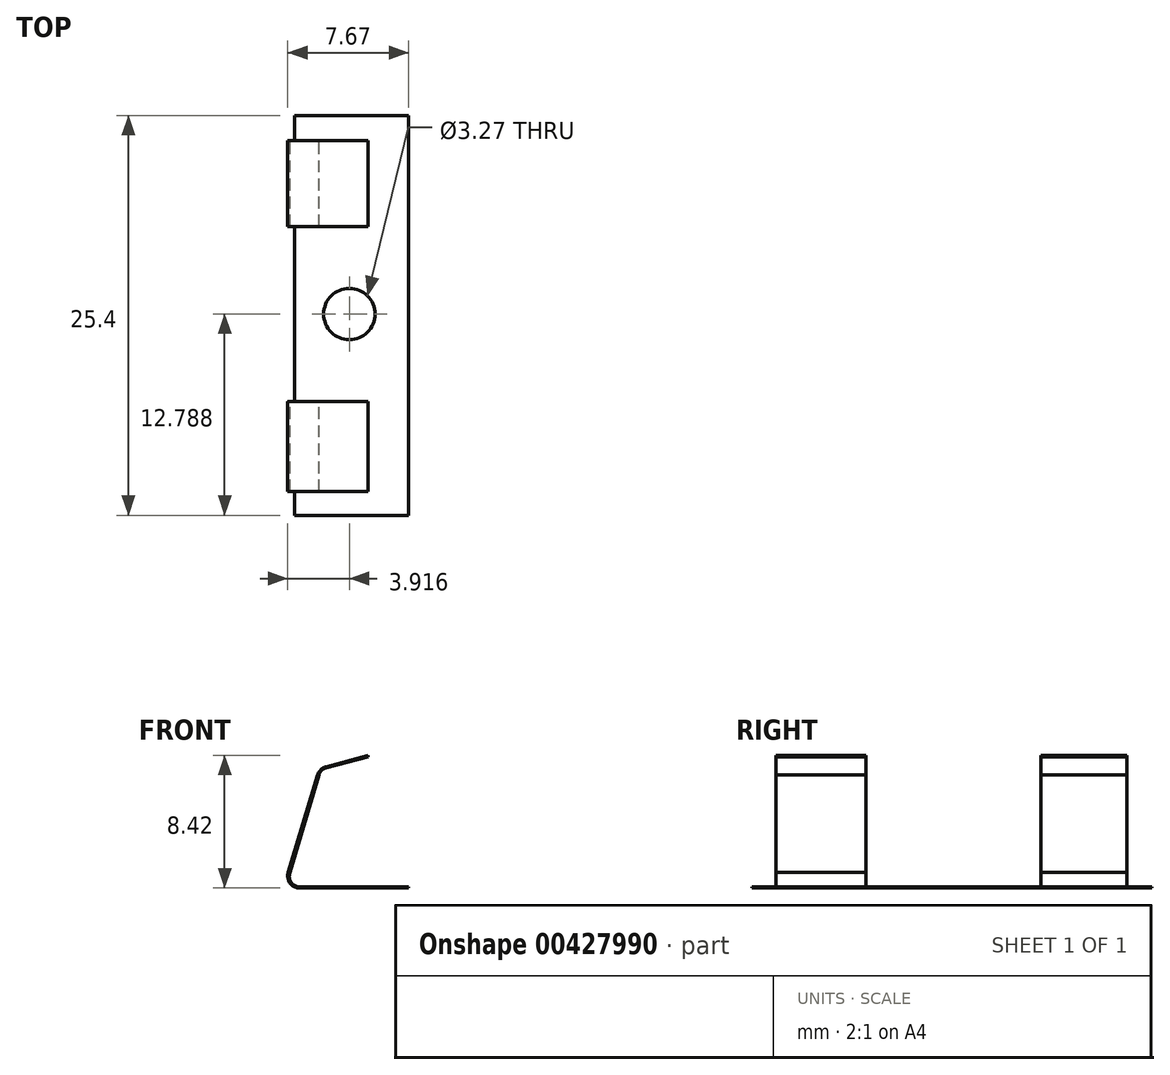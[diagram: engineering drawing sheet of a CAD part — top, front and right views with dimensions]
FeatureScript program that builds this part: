
annotation { "Feature Type Name" : "Feature", "Feature Type Description" : "" }
export const myFeature = defineFeature(function(context is Context, id is Id, definition is map)
    precondition{}
    {
        {
            var Q0;
            Q0=qCreatedBy(makeId("Front.planeOp"),FACE);
            var sketch = newSketch(context, id + "F0", { "sketchPlane" : qUnion([Q0])});
            skLineSegment(sketch, "E0", {"start": v(0, 0) * mm, "end": v(-0.56, 0) * mm});
            skLineSegment(sketch, "E1", {"start": v(-1.3, 0.98) * mm, "end": v(0.59, 7.2) * mm});
            skLineSegment(sketch, "E2", {"start": v(0, 0) * mm, "end": v(6.35, 0) * mm});
            skLineSegment(sketch, "E3", {"start": v(1.12, 7.7) * mm, "end": v(3.78, 8.42) * mm});
            skPoint(sketch, "E4.visualSharp", {"position": v(0.7, 7.6) * mm});
            skArc(sketch, "E4.filletArc", {"start": v(1.12, 7.7) * mm, "mid": v(0.79, 7.52) * mm, "end": v(0.59, 7.2) * mm});
            skPoint(sketch, "E5.visualSharp", {"position": v(-1.59, 0) * mm});
            skArc(sketch, "E5.filletArc", {"start": v(-1.3, 0.98) * mm, "mid": v(-1.17, 0.3) * mm, "end": v(-0.56, 0) * mm});
            skLineSegment(sketch, "E6", {"start": v(6.35, 0) * mm, "end": v(6.35, 0.08) * mm});
            skLineSegment(sketch, "E7", {"start": v(3.78, 8.42) * mm, "end": v(3.78, 8.34) * mm});
            skLineSegment(sketch, "E8", {"start": v(3.78, 8.34) * mm, "end": v(1.12, 7.63) * mm});
            skLineSegment(sketch, "E9", {"start": v(6.35, 0.08) * mm, "end": v(-0.56, 0.08) * mm});
            skArc(sketch, "E10", {"start": v(-1.17, 0.98) * mm, "mid": v(-1.1, 0.37) * mm, "end": v(-0.56, 0.08) * mm});
            skPoint(sketch, "E10.startSnap0", {"position": v(-1.17, 0.3) * mm});
            skArc(sketch, "E11", {"start": v(1.12, 7.63) * mm, "mid": v(0.83, 7.47) * mm, "end": v(0.66, 7.2) * mm});
            skLineSegment(sketch, "E12", {"start": v(0.66, 7.2) * mm, "end": v(-1.17, 0.98) * mm});
            skSolve(sketch);
        }
        {
            var Q0;
            Q0=makeQuery(id+"F0.imprint","IMPRINT",FACE,{"disambiguationData":[TD([[makeQuery(id+"F0.imprint","IMPRINT",EDGE,{"derivedFrom":sQuery(id+"F0.wireOp",EDGE,"E0")}),-1.0]])]});
            extrude(context, id + "F1", {"entities" : qUnion([Q0]), "depth" : 25.4 * mm});
        }
        {
            var Q0;
            Q0=qCreatedBy(makeId("Top.planeOp"),FACE);
            cPlane(context, id + "F2", {"entities" : qUnion([Q0]), "cplaneType" : CPlaneType.OFFSET, "offset" : 0.08 * mm, "width" : 152.4 * mm, "height" : 152.4 * mm});
        }
        {
            var Q0;
            Q0=qCreatedBy(id+"F2.planeOp",FACE);
            var sketch = newSketch(context, id + "F3", { "sketchPlane" : qUnion([Q0])});
            skLineSegment(sketch, "E13.bottom", {"start": v(-2.67, -7.06) * mm, "end": v(5.48, -7.06) * mm});
            skLineSegment(sketch, "E13.top", {"start": v(-2.67, -18.17) * mm, "end": v(5.48, -18.17) * mm});
            skLineSegment(sketch, "E13.left", {"start": v(-2.67, -7.06) * mm, "end": v(-2.67, -18.17) * mm});
            skLineSegment(sketch, "E13.right", {"start": v(5.48, -7.06) * mm, "end": v(5.48, -18.17) * mm});
            skLineSegment(sketch, "E14.bottom", {"start": v(4.88, 0) * mm, "end": v(-3.06, 0) * mm});
            skLineSegment(sketch, "E14.top", {"start": v(4.88, -1.59) * mm, "end": v(-3.06, -1.59) * mm});
            skLineSegment(sketch, "E14.left", {"start": v(4.88, 0) * mm, "end": v(4.88, -1.59) * mm});
            skLineSegment(sketch, "E14.right", {"start": v(-3.06, 0) * mm, "end": v(-3.06, -1.59) * mm});
            skLineSegment(sketch, "E15", {"start": v(-2.67, -12.61) * mm, "end": v(13.38, -12.61) * mm});
            skPoint(sketch, "E15.endSnap0", {"position": v(-2.67, -12.61) * mm});
            skLineSegment(sketch, "E16.bottom", {"start": v(-1.4, -25.47) * mm, "end": v(7.45, -25.47) * mm});
            skLineSegment(sketch, "E16.top", {"start": v(-1.4, -23.88) * mm, "end": v(7.45, -23.88) * mm});
            skLineSegment(sketch, "E16.left", {"start": v(-1.4, -25.47) * mm, "end": v(-1.4, -23.88) * mm});
            skLineSegment(sketch, "E16.right", {"start": v(7.45, -25.47) * mm, "end": v(7.45, -23.88) * mm});
            skSolve(sketch);
        }
        {
            var Q0;
            Q0=makeQuery(id+"F3.imprint","IMPRINT",FACE,{"disambiguationData":[TD([[makeQuery(id+"F3.imprint","IMPRINT",EDGE,{"derivedFrom":sQuery(id+"F3.wireOp",EDGE,"E13.bottom")}),-1.0]])]});
            var Q1;
            Q1=makeQuery(id+"F3.imprint","IMPRINT",FACE,{"disambiguationData":[TD([[makeQuery(id+"F3.imprint","IMPRINT",EDGE,{"derivedFrom":sQuery(id+"F3.wireOp",EDGE,"E14.bottom")}),1.0]])]});
            var Q2;
            Q2=makeQuery(id+"F3.imprint","IMPRINT",FACE,{"disambiguationData":[TD([[makeQuery(id+"F3.imprint","IMPRINT",EDGE,{"derivedFrom":sQuery(id+"F3.wireOp",EDGE,"E16.bottom")}),1.0]])]});
            var Q3;
            {var subQ0=sQuery(id+"F3.wireOp",EDGE,"E13.top");Q3=makeQuery(id+"F3.imprint","IMPRINT",FACE,{"disambiguationData":[TD([[makeQuery(id+"F3.imprint","IMPRINT",EDGE,{"derivedFrom":subQ0}),1.0]])]});}
            extrude(context, id + "F4", {"entities" : qUnion([Q0, Q1, Q2, Q3]), "operationType" : NewBodyOperationType.REMOVE, "depth" : 25.4 * mm});
        }
        {
            var Q0;
            Q0=makeQuery(id+"F4.boolean.opBoolean","MERGE",FACE,{"derivedFrom":[makeQuery(id+"F1.opExtrude","SWEPT_FACE",FACE,{"disambiguationData":[OSD([sQuery(id+"F0.wireOp",EDGE,"E9")])]}),makeQuery(id+"F4.opExtrude","CAP_FACE",FACE,{"disambiguationData":[OSD([sQuery(id+"F3.wireOp",EDGE,"E13.bottom"),sQuery(id+"F3.wireOp",EDGE,"E13.top"),sQuery(id+"F3.wireOp",EDGE,"E13.left"),sQuery(id+"F3.wireOp",EDGE,"E13.right")])],"isStart":true}),makeQuery(id+"F4.opExtrude","CAP_FACE",FACE,{"disambiguationData":[OSD([sQuery(id+"F3.wireOp",EDGE,"E14.bottom"),sQuery(id+"F3.wireOp",EDGE,"E14.top"),sQuery(id+"F3.wireOp",EDGE,"E14.left"),sQuery(id+"F3.wireOp",EDGE,"E14.right")])],"isStart":true}),makeQuery(id+"F4.opExtrude","CAP_FACE",FACE,{"disambiguationData":[OSD([sQuery(id+"F3.wireOp",EDGE,"E16.bottom"),sQuery(id+"F3.wireOp",EDGE,"E16.top"),sQuery(id+"F3.wireOp",EDGE,"E16.left"),sQuery(id+"F3.wireOp",EDGE,"E16.right")])],"isStart":true})]});
            var sketch = newSketch(context, id + "F5", { "sketchPlane" : qUnion([Q0])});
            skCircle(sketch, "E17", {"center": v(2.6, -12.61) * mm, "radius": 1.63 * mm});
            skPoint(sketch, "E17.centerSnap0", {"position": v(-0.9, -12.61) * mm});
            skSolve(sketch);
        }
        {
            var Q0;
            Q0 = qSketchRegion(id + "F5", true);
            extrude(context, id + "F6", {"entities" : qUnion([Q0]), "operationType" : NewBodyOperationType.REMOVE, "oppositeDirection" : true, "depth" : 25.4 * mm});
        }
    });
